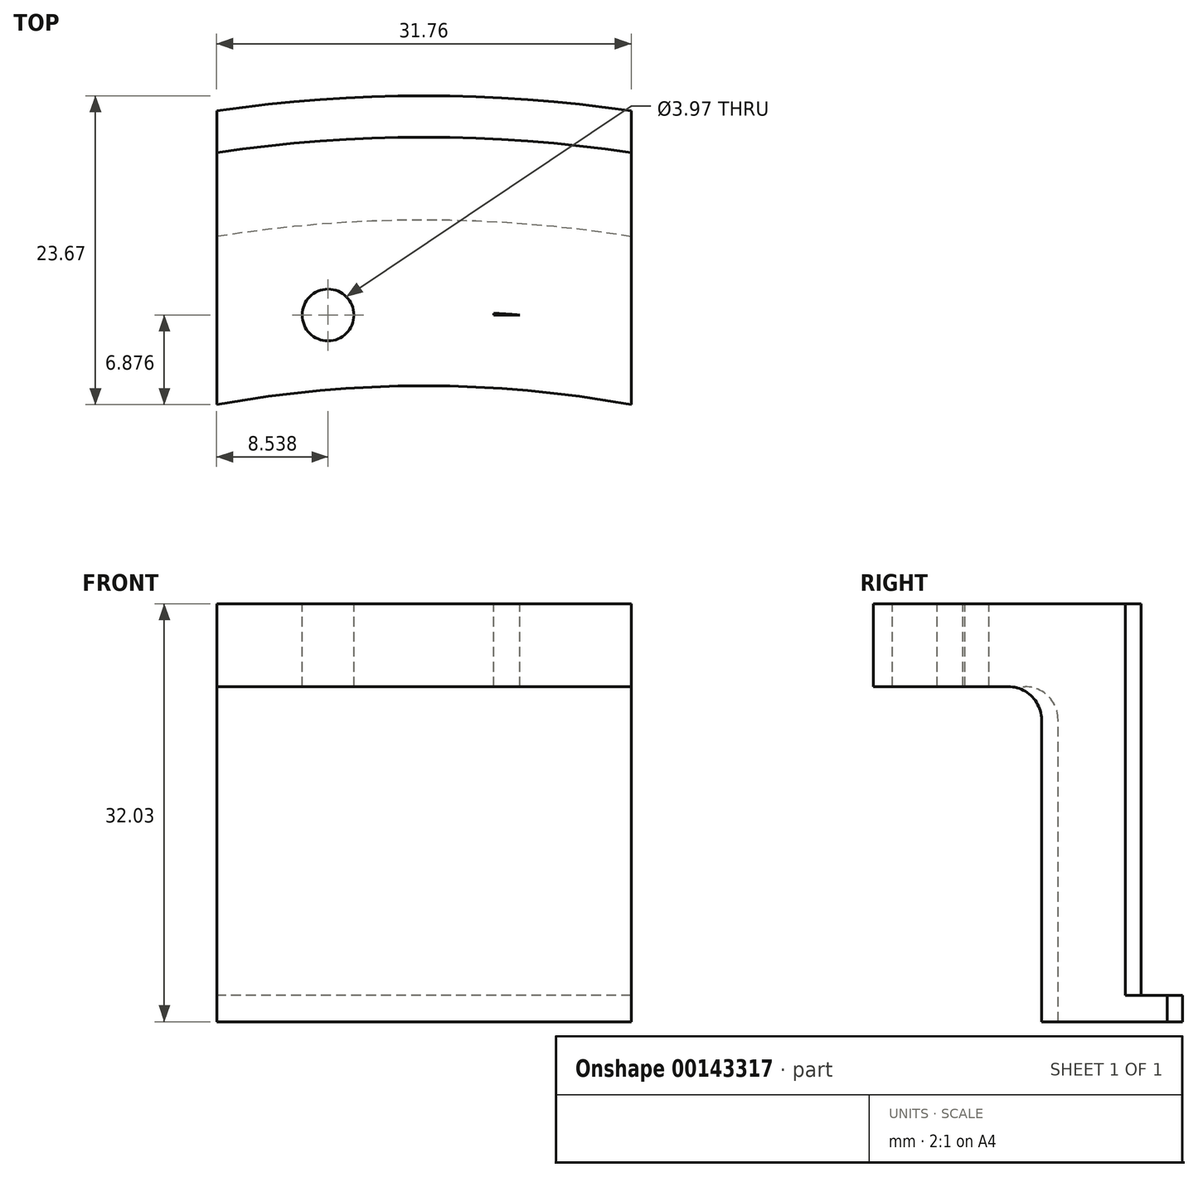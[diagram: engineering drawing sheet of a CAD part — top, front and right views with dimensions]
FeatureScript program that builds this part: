
annotation { "Feature Type Name" : "Feature", "Feature Type Description" : "" }
export const myFeature = defineFeature(function(context is Context, id is Id, definition is map)
    precondition{}
    {
        {
            var Q0;
            Q0=qCreatedBy(makeId("Right.planeOp"),FACE);
            var sketch = newSketch(context, id + "F0", { "sketchPlane" : qUnion([Q0])});
            skLineSegment(sketch, "E0", {"start": v(0, 0) * mm, "end": v(-106.68, 0) * mm});
            skLineSegment(sketch, "E1", {"start": v(-106.68, 0) * mm, "end": v(-106.68, -30) * mm});
            skLineSegment(sketch, "E2", {"start": v(-106.68, -30) * mm, "end": v(-109.86, -30) * mm});
            skLineSegment(sketch, "E3", {"start": v(-109.86, -30) * mm, "end": v(-109.86, -32.03) * mm});
            skLineSegment(sketch, "E4", {"start": v(-109.86, -32.03) * mm, "end": v(-100.33, -32.03) * mm});
            skLineSegment(sketch, "E5", {"start": v(-100.33, -32.03) * mm, "end": v(-100.33, -6.35) * mm});
            skLineSegment(sketch, "E6", {"start": v(-100.33, -6.35) * mm, "end": v(-87.63, -6.35) * mm});
            skLineSegment(sketch, "E7", {"start": v(-87.63, -6.35) * mm, "end": v(-87.63, 0) * mm});
            skLineSegment(sketch, "E8", {"start": v(-87.63, 0) * mm, "end": v(-106.68, 0) * mm});
            skLineSegment(sketch, "E9", {"start": v(0, 0) * mm, "end": v(0, -69.66) * mm});
            skSolve(sketch);
        }
        {
            var Q0;
            Q0=makeQuery(id+"F0.imprint","IMPRINT",FACE,{"disambiguationData":[TD([[makeQuery(id+"F0.imprint","IMPRINT",EDGE,{"derivedFrom":sQuery(id+"F0.wireOp",EDGE,"E1")}),1.0]])]});
            var Q1;
            Q1=sQuery(id+"F0.wireOp",EDGE,"E9");
            revolve(context, id + "F1", {"surfaceOperationType" : NewSurfaceOperationType.NEW, "entities" : qUnion([Q0]), "axis" : qUnion([Q1]), "revolveType" : RevolveType.FULL});
        }
        {
            var Q0;
            Q0=qCreatedBy(makeId("Top.planeOp"),FACE);
            var sketch = newSketch(context, id + "F2", { "sketchPlane" : qUnion([Q0])});
            skLineSegment(sketch, "E10.bottom", {"start": v(15.88, -145.58) * mm, "end": v(-15.87, -145.58) * mm});
            skLineSegment(sketch, "E10.top", {"start": v(15.88, 145.58) * mm, "end": v(-15.87, 145.58) * mm});
            skLineSegment(sketch, "E10.left", {"start": v(15.88, -145.58) * mm, "end": v(15.88, 145.58) * mm});
            skLineSegment(sketch, "E10.right", {"start": v(-15.88, -145.58) * mm, "end": v(-15.87, 145.58) * mm});
            skPoint(sketch, "E10.middle", {"position": v(0, 0) * mm});
            skLineSegment(sketch, "E11.bottom", {"start": v(134.21, 134.25) * mm, "end": v(-134.21, 134.25) * mm});
            skLineSegment(sketch, "E11.top", {"start": v(134.21, -134.25) * mm, "end": v(-134.21, -134.25) * mm});
            skLineSegment(sketch, "E11.left", {"start": v(134.21, 134.25) * mm, "end": v(134.21, -134.25) * mm});
            skLineSegment(sketch, "E11.right", {"start": v(-134.21, 134.25) * mm, "end": v(-134.21, -134.25) * mm});
            skLineSegment(sketch, "E12", {"start": v(-15.87, 0) * mm, "end": v(15.88, 0) * mm});
            skLineSegment(sketch, "E13", {"start": v(-15.87, 76.2) * mm, "end": v(15.88, 76.2) * mm});
            skLineSegment(sketch, "E14", {"start": v(15.88, 76.2) * mm, "end": v(-15.87, 76.2) * mm});
            skSolve(sketch);
        }
        {
            var Q0;
            {var subQ4=sQuery(id+"F2.wireOp",EDGE,"E11.right");Q0=makeQuery(id+"F2.imprint","IMPRINT",FACE,{"disambiguationData":[TD([[makeQuery(id+"F2.imprint","IMPRINT",EDGE,{"derivedFrom":subQ4}),1.0]])]});}
            var Q1;
            {var subQ0=sQuery(id+"F2.wireOp",EDGE,"E11.left");Q1=makeQuery(id+"F2.imprint","IMPRINT",FACE,{"disambiguationData":[TD([[makeQuery(id+"F2.imprint","IMPRINT",EDGE,{"derivedFrom":subQ0}),-1.0]])]});}
            var Q2;
            {var subQ0=sQuery(id+"F2.wireOp",EDGE,"E12");Q2=makeQuery(id+"F2.imprint","IMPRINT",FACE,{"disambiguationData":[TD([[makeQuery(id+"F2.imprint","IMPRINT",EDGE,{"derivedFrom":subQ0}),1.0]])]});}
            var Q3;
            {var subQ0=sQuery(id+"F2.wireOp",EDGE,"E12");Q3=makeQuery(id+"F2.imprint","IMPRINT",FACE,{"disambiguationData":[TD([[makeQuery(id+"F2.imprint","IMPRINT",EDGE,{"derivedFrom":subQ0}),-1.0]])]});}
            extrude(context, id + "F3", {"entities" : qUnion([Q0, Q1, Q2, Q3]), "operationType" : NewBodyOperationType.REMOVE, "endBound" : BoundingType.THROUGH_ALL, "oppositeDirection" : true, "depth" : 25.4 * mm, "offsetDistance" : 25.4 * mm});
        }
        {
            var Q0;
            Q0=makeQuery(id+"F1.opRevolve","SWEPT_EDGE",EDGE,{"disambiguationData":[OSD([sQuery(id+"F0.wireOp",EDGE,"E5"),sQuery(id+"F0.wireOp",EDGE,"E6")])]});
            fillet(context, id + "F4", {"entities" : qUnion([Q0]), "radius" : 2.54 * mm, "tangentPropagation" : true, "allowEdgeOverflow" : false});
        }
        {
            var Q0;
            Q0=qCreatedBy(makeId("Top.planeOp"),FACE);
            var sketch = newSketch(context, id + "F5", { "sketchPlane" : qUnion([Q0])});
            skCircle(sketch, "E15", {"center": v(0, 0) * mm, "radius": 93.35 * mm});
            skCircle(sketch, "E16", {"center": v(-7.34, 93.06) * mm, "radius": 1.98 * mm});
            skCircle(sketch, "E17", {"center": v(7.34, 93.06) * mm, "radius": 1.98 * mm});
            skLineSegment(sketch, "E18", {"start": v(-7.34, 93.06) * mm, "end": v(7.34, 93.06) * mm});
            skLineSegment(sketch, "E19", {"start": v(0, 0) * mm, "end": v(0, 93.35) * mm});
            skPoint(sketch, "E20", {"position": v(0, 93.06) * mm});
            skSolve(sketch);
        }
        {
            var Q0;
            {var subQ0=sQuery(id+"F5.wireOp",EDGE,"E16");var subQ1=sQuery(id+"F5.wireOp",EDGE,"E15");var subQ2=makeQuery(id+"F5.imprint","INTERSECT",VERTEX,{"disambiguationData":[OD(0.0)],"derivedFrom":[subQ1,subQ0]});Q0=makeQuery(id+"F5.imprint","IMPRINT",FACE,{"disambiguationData":[TD([[makeQuery(id+"F5.imprint","IMPRINT",EDGE,{"disambiguationData":[TD([[subQ2,-1.0]])],"derivedFrom":subQ1}),-1.0]])]});}
            var Q1;
            {var subQ0=sQuery(id+"F5.wireOp",EDGE,"E16");var subQ1=sQuery(id+"F5.wireOp",EDGE,"E15");var subQ2=makeQuery(id+"F5.imprint","INTERSECT",VERTEX,{"disambiguationData":[OD(0.0)],"derivedFrom":[subQ1,subQ0]});Q1=makeQuery(id+"F5.imprint","IMPRINT",FACE,{"disambiguationData":[TD([[makeQuery(id+"F5.imprint","IMPRINT",EDGE,{"disambiguationData":[TD([[subQ2,-1.0]])],"derivedFrom":subQ1}),1.0]])]});}
            var Q2;
            {var subQ0=sQuery(id+"F5.wireOp",EDGE,"E17");var subQ1=sQuery(id+"F5.wireOp",EDGE,"E15");var subQ2=makeQuery(id+"F5.imprint","INTERSECT",VERTEX,{"disambiguationData":[OD(0.0)],"derivedFrom":[subQ1,subQ0]});Q2=makeQuery(id+"F5.imprint","IMPRINT",FACE,{"disambiguationData":[TD([[makeQuery(id+"F5.imprint","IMPRINT",EDGE,{"disambiguationData":[TD([[subQ2,1.0]])],"derivedFrom":subQ1}),-1.0]])]});}
            var Q3;
            {var subQ0=sQuery(id+"F5.wireOp",EDGE,"E18");var subQ1=sQuery(id+"F5.wireOp",EDGE,"E15");var subQ2=makeQuery(id+"F5.imprint","INTERSECT",VERTEX,{"disambiguationData":[OD(0.0)],"derivedFrom":[subQ1,subQ0]});Q3=makeQuery(id+"F5.imprint","IMPRINT",FACE,{"disambiguationData":[TD([[makeQuery(id+"F5.imprint","IMPRINT",EDGE,{"disambiguationData":[TD([[subQ2,-1.0]])],"derivedFrom":subQ1}),1.0]])]});}
            var Q4;
            {var subQ0=sQuery(id+"F5.wireOp",EDGE,"E15");var subQ1=makeQuery(id+"F5.imprint","INTERSECT",VERTEX,{"disambiguationData":[OD(1.0)],"derivedFrom":[subQ0,sQuery(id+"F5.wireOp",EDGE,"E18")]});Q4=makeQuery(id+"F5.imprint","IMPRINT",FACE,{"disambiguationData":[TD([[makeQuery(id+"F5.imprint","IMPRINT",EDGE,{"disambiguationData":[TD([[subQ1,1.0]])],"derivedFrom":subQ0}),-1.0]])]});}
            var Q5;
            {var subQ0=sQuery(id+"F5.wireOp",EDGE,"E18");var subQ1=sQuery(id+"F5.wireOp",EDGE,"E15");var subQ2=makeQuery(id+"F5.imprint","INTERSECT",VERTEX,{"disambiguationData":[OD(1.0)],"derivedFrom":[subQ1,subQ0]});Q5=makeQuery(id+"F5.imprint","IMPRINT",FACE,{"disambiguationData":[TD([[makeQuery(id+"F5.imprint","IMPRINT",EDGE,{"disambiguationData":[TD([[subQ2,1.0]])],"derivedFrom":subQ1}),1.0]])]});}
            var Q6;
            {var subQ0=sQuery(id+"F5.wireOp",EDGE,"E18");var subQ1=sQuery(id+"F5.wireOp",EDGE,"E15");var subQ2=makeQuery(id+"F5.imprint","INTERSECT",VERTEX,{"disambiguationData":[OD(1.0)],"derivedFrom":[subQ1,subQ0]});Q6=makeQuery(id+"F5.imprint","IMPRINT",FACE,{"disambiguationData":[TD([[makeQuery(id+"F5.imprint","IMPRINT",EDGE,{"disambiguationData":[TD([[subQ2,-1.0]])],"derivedFrom":subQ1}),1.0]])]});}
            extrude(context, id + "F6", {"entities" : qUnion([Q0, Q1, Q2, Q3, Q4, Q5, Q6]), "operationType" : NewBodyOperationType.REMOVE, "endBound" : BoundingType.THROUGH_ALL, "oppositeDirection" : true, "depth" : 25.4 * mm, "offsetDistance" : 25.4 * mm});
        }
    });
